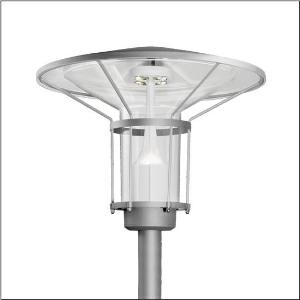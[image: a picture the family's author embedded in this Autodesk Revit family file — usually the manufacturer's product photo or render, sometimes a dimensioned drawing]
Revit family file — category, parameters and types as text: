
# Revit family: laterne_classic_iq___p1_0a_5xa5245ff14h_a382
name_source: partatom
category: Lighting Fixtures
units: mm (PartAtom-declared; Revit-internal decimal feet)

## family parameters
Cut with Voids When Loaded = No
Host = Face
Light Source = No
Part Type = Normal
Room Calculation Point = No
Round Connector Dimension = Use Diameter
Shared = No

## types (1)
- --- (1 x LED, 1360 lm, 10.5 W, 3000K)
    Apparent Load = 11 VA
    CIE Flux Codes = 30 61 91 96 100
    Color Rendering = 70
    Color Temperature = 3000K
    Default Elevation = 1800 mm
    Description = Lantern Classic iQ, mast luminaire, Module 540 iQ-SR, primary light control with 3 zone facetted reflector, of plastic, silver coated, highly specular, structured, primary optical cover: cover, of PMMA, transparent, light distribution: P1.0a, light emission: direct distribution, primary light characteristic: strongly asymmetric, installation type: post-top, LED, High Power LED, rated luminous flux: 1.360lm, luminous efficacy: 130lm/W, light colour: 730, colour temperature: 3000K, control gear: ECG iQ, control: Auto-Match, Temp-Guard, Lumen-Switch, Night-Set, Smart-Wire, Light-Fading, Desk-Remote (wireless, voltage-free reading and setting of iQ features in the workshop via application-optimized NFC function/RFID function), optimised constant luminous flux control (CLO 2.0), Street-Remote, presetting dimming logarithmic, with terminal, 6-pole, max. 2.5mm², mains connection: 230..240V, AC, 50/60Hz, start of lifetime: 11W, end of service life: 11W, reduction: 5W, luminaire housing, upper part, of glass-fibre reinforced polyester, coated, Siteco® metallic grey (DB 702S), diameter: 750mm, height: 596mm, spigot size: d x l = 76 x 70mm (post-top) | with reducer (optional accessory) 60 x 70mm, post-top mast mounting element, of diecast aluminium, coated, Siteco® metallic grey (DB 702S), Module 540 iQ-SR, traffic white (RAL 9016), equipment: standard, protection rating (complete): IP65, insulation class (complete): insulation class II (safety insulation), certification: CE, ENEC, VDE, packaging unit: 1 piece

Light Distribution: P1.0a
    Height = 596 mm
    Lamp = 1 x LED
    Lamp Light Flux = 1360 lm
    Lamp Power = 10.5 W
    Lamp count = 1
    Length = 750 mm
    Luminous efficacy = 130 lm/W
    Manufacturer = Siteco
    ModVariant = No
    Model = 5XA5245FF14H
    Number of Poles = 1
    OnlyDefault = Yes
    Power Factor = 1
    Product Name = Laterne Classic iQ | P1.0a
    Product group = mast luminaire | pylon top
    ProductGroupID = 6100
    Protection Class = Protection class II
    Protection Degree = IP 65
    RLX_Detail_Level = 1
    RLX_Emergency_Light_Flux = 0 lm
    RLX_Emergency_Type = 0
    RLX_Emergency_Type_DB = No
    RlxData = <blob elided: 93813 chars, md5=662552fe>
    Socket = socket
    Standby Power = 0 W
    System Light Flux = 1360 lm
    System Power = 11 W
    Type Comments = factory setting: luminous flux: 100 % | dim-lin: 254 | 419 mA
    Type Image = l_1006052.jpg
    URL = http://relux.com
    VarID = @adj_110421
    Voltage = 0 V
    Weight = 0.00 kg
    Width = 0 mm  [stored 0 ft]

note: [stored X ft] marks values corroborated as IEEE doubles in the binary element streams (Revit-internal decimal feet)

## geometry (parser evidence)
native form markers: Blend x4, Sweep x10
no freeform markers — native parametric forms only
